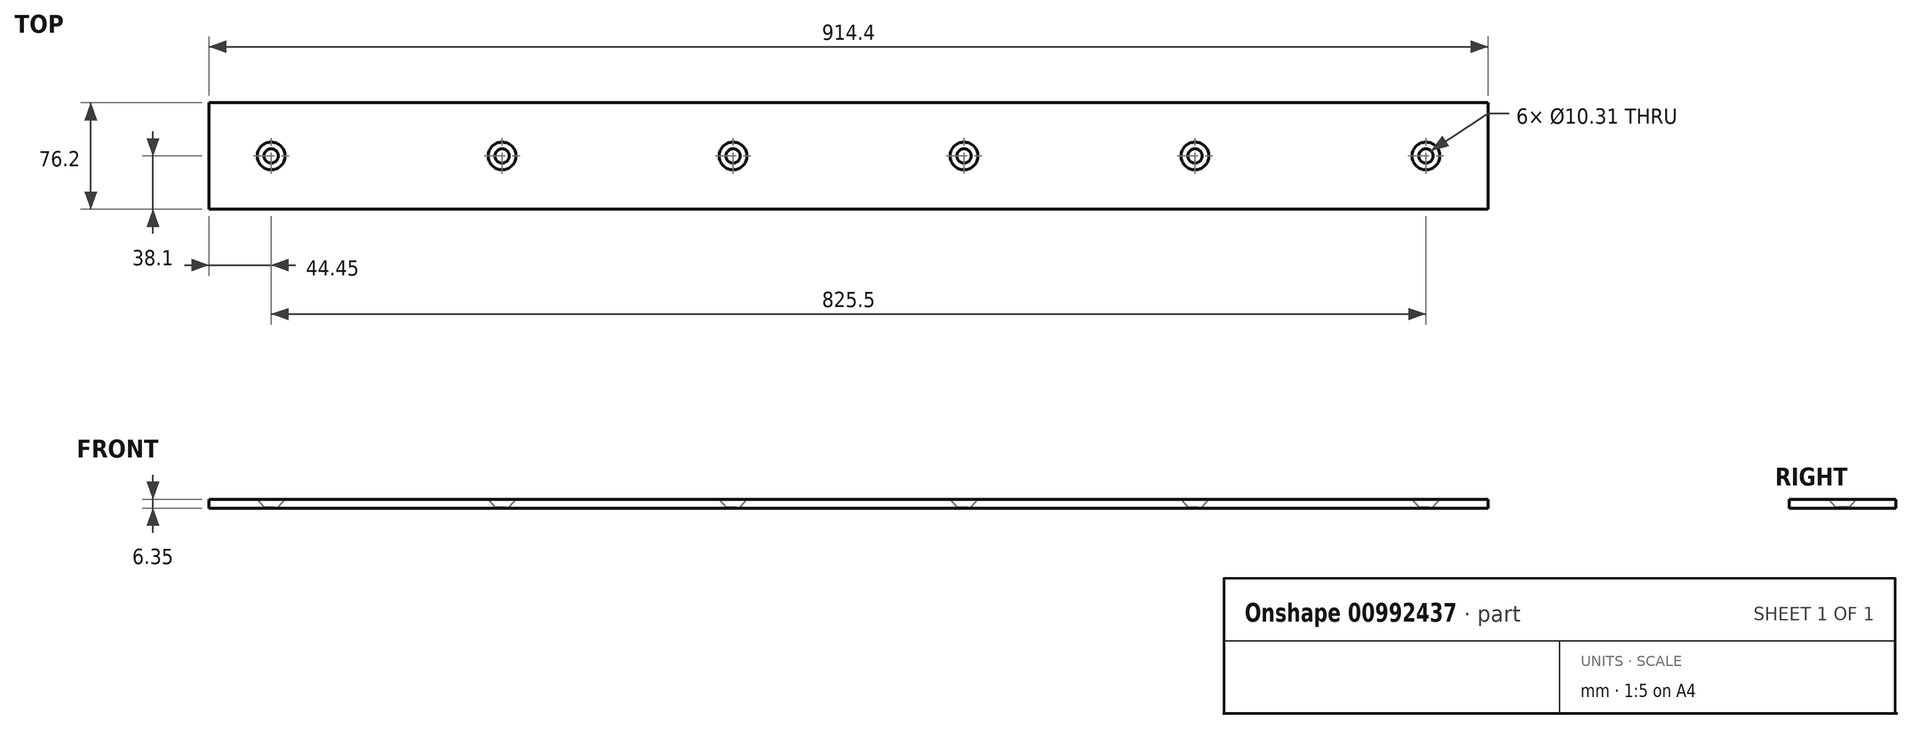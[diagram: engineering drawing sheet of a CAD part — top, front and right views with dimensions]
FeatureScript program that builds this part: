
annotation { "Feature Type Name" : "Feature", "Feature Type Description" : "" }
export const myFeature = defineFeature(function(context is Context, id is Id, definition is map)
    precondition{}
    {
        {
            var Q0;
            Q0=qCreatedBy(makeId("Top.planeOp"),FACE);
            var sketch = newSketch(context, id + "F0", { "sketchPlane" : qUnion([Q0])});
            skLineSegment(sketch, "E0.bottom", {"start": v(457.2, 38.1) * mm, "end": v(-457.2, 38.1) * mm});
            skLineSegment(sketch, "E0.top", {"start": v(457.2, -38.1) * mm, "end": v(-457.2, -38.1) * mm});
            skLineSegment(sketch, "E0.left", {"start": v(457.2, 38.1) * mm, "end": v(457.2, -38.1) * mm});
            skLineSegment(sketch, "E0.right", {"start": v(-457.2, 38.1) * mm, "end": v(-457.2, -38.1) * mm});
            skPoint(sketch, "E0.middle", {"position": v(0, 0) * mm});
            skCircle(sketch, "E1", {"center": v(-412.75, 0) * mm, "radius": 4.76 * mm});
            skPoint(sketch, "E1.centerSnap0", {"position": v(-457.2, 0) * mm});
            skCircle(sketch, "E2.1.0.0", {"center": v(-247.65, 0) * mm, "radius": 4.76 * mm});
            skCircle(sketch, "E2.2.0.0", {"center": v(-82.55, 0) * mm, "radius": 4.76 * mm});
            skCircle(sketch, "E2.3.0.0", {"center": v(82.55, 0) * mm, "radius": 4.76 * mm});
            skCircle(sketch, "E2.4.0.0", {"center": v(247.65, 0) * mm, "radius": 4.76 * mm});
            skCircle(sketch, "E2.5.0.0", {"center": v(412.75, 0) * mm, "radius": 4.76 * mm});
            skLineSegment(sketch, "E2.direction1", {"start": v(-412.75, 0) * mm, "end": v(-247.65, 0) * mm, "construction": true});
            skSolve(sketch);
        }
        {
            var Q0;
            Q0=makeQuery(id+"F0.imprint","IMPRINT",FACE,{"disambiguationData":[TD([[makeQuery(id+"F0.imprint","IMPRINT",EDGE,{"derivedFrom":sQuery(id+"F0.wireOp",EDGE,"E0.bottom")}),1.0]])]});
            var Q1;
            Q1=makeQuery(id+"F0.imprint","IMPRINT",FACE,{"disambiguationData":[TD([[makeQuery(id+"F0.imprint","IMPRINT",EDGE,{"derivedFrom":sQuery(id+"F0.wireOp",EDGE,"E2.2.0.0")}),1.0]])]});
            var Q2;
            Q2=makeQuery(id+"F0.imprint","IMPRINT",FACE,{"disambiguationData":[TD([[makeQuery(id+"F0.imprint","IMPRINT",EDGE,{"derivedFrom":sQuery(id+"F0.wireOp",EDGE,"E2.3.0.0")}),1.0]])]});
            var Q3;
            Q3=makeQuery(id+"F0.imprint","IMPRINT",FACE,{"disambiguationData":[TD([[makeQuery(id+"F0.imprint","IMPRINT",EDGE,{"derivedFrom":sQuery(id+"F0.wireOp",EDGE,"E2.4.0.0")}),1.0]])]});
            var Q4;
            Q4=makeQuery(id+"F0.imprint","IMPRINT",FACE,{"disambiguationData":[TD([[makeQuery(id+"F0.imprint","IMPRINT",EDGE,{"derivedFrom":sQuery(id+"F0.wireOp",EDGE,"E2.5.0.0")}),1.0]])]});
            var Q5;
            Q5=makeQuery(id+"F0.imprint","IMPRINT",FACE,{"disambiguationData":[TD([[makeQuery(id+"F0.imprint","IMPRINT",EDGE,{"derivedFrom":sQuery(id+"F0.wireOp",EDGE,"E1")}),1.0]])]});
            var Q6;
            Q6=makeQuery(id+"F0.imprint","IMPRINT",FACE,{"disambiguationData":[TD([[makeQuery(id+"F0.imprint","IMPRINT",EDGE,{"derivedFrom":sQuery(id+"F0.wireOp",EDGE,"E2.1.0.0")}),1.0]])]});
            extrude(context, id + "F1", {"entities" : qUnion([Q0, Q1, Q2, Q3, Q4, Q5, Q6]), "oppositeDirection" : true, "depth" : 6.35 * mm, "offsetDistance" : 25.4 * mm});
        }
        {
            var Q0;
            Q0=sQuery(id+"F0.wireOp",VERTEX,"E2.direction1.start");
            var Q1;
            Q1=sQuery(id+"F0.wireOp",VERTEX,"E2.direction1.end");
            var Q2;
            Q2=sQuery(id+"F0.wireOp",VERTEX,"E2.2.0.0.center");
            var Q3;
            Q3=sQuery(id+"F0.wireOp",VERTEX,"E2.3.0.0.center");
            var Q4;
            Q4=sQuery(id+"F0.wireOp",VERTEX,"E2.4.0.0.center");
            var Q5;
            Q5=sQuery(id+"F0.wireOp",VERTEX,"E2.5.0.0.center");
            var Q6;
            Q6=makeQuery(id+"F1.opExtrude","SWEPT_BODY",BODY,{"disambiguationData":[OSD([sQuery(id+"F0.wireOp",EDGE,"E0.bottom"),sQuery(id+"F0.wireOp",EDGE,"E0.top"),sQuery(id+"F0.wireOp",EDGE,"E0.left"),sQuery(id+"F0.wireOp",EDGE,"E0.right")])]});
            hole(context, id + "F2", {"style" : HoleStyle.C_SINK, "endStyle" : HoleEndStyle.THROUGH, "standardTappedOrClearance" : lookupTablePath({ "fit" : "Normal (ASME)", "standard" : "ANSI", "size" : "3/8", "type" : "Clearance" }), "standardBlindInLast" : lookupTablePath({ "fit" : "Normal", "standard" : "ANSI", "engagement" : "75%", "pitch" : "16 tpi", "size" : "3/8", "type" : "Clearance & tapped" }), "holeDiameter" : 10.3 * mm, "cSinkDiameter" : 19.84 * mm, "cSinkAngle" : 82 * degree, "majorDiameter" : 6.35 * mm, "isTappedThrough" : true, "tappedDepth" : 12.7 * mm, "tapClearance" : 3, "locations" : qUnion([Q0, Q1, Q2, Q3, Q4, Q5]), "scope" : qUnion([Q6]), "startStyle" : HoleStartStyle.SKETCH});
        }
    });
